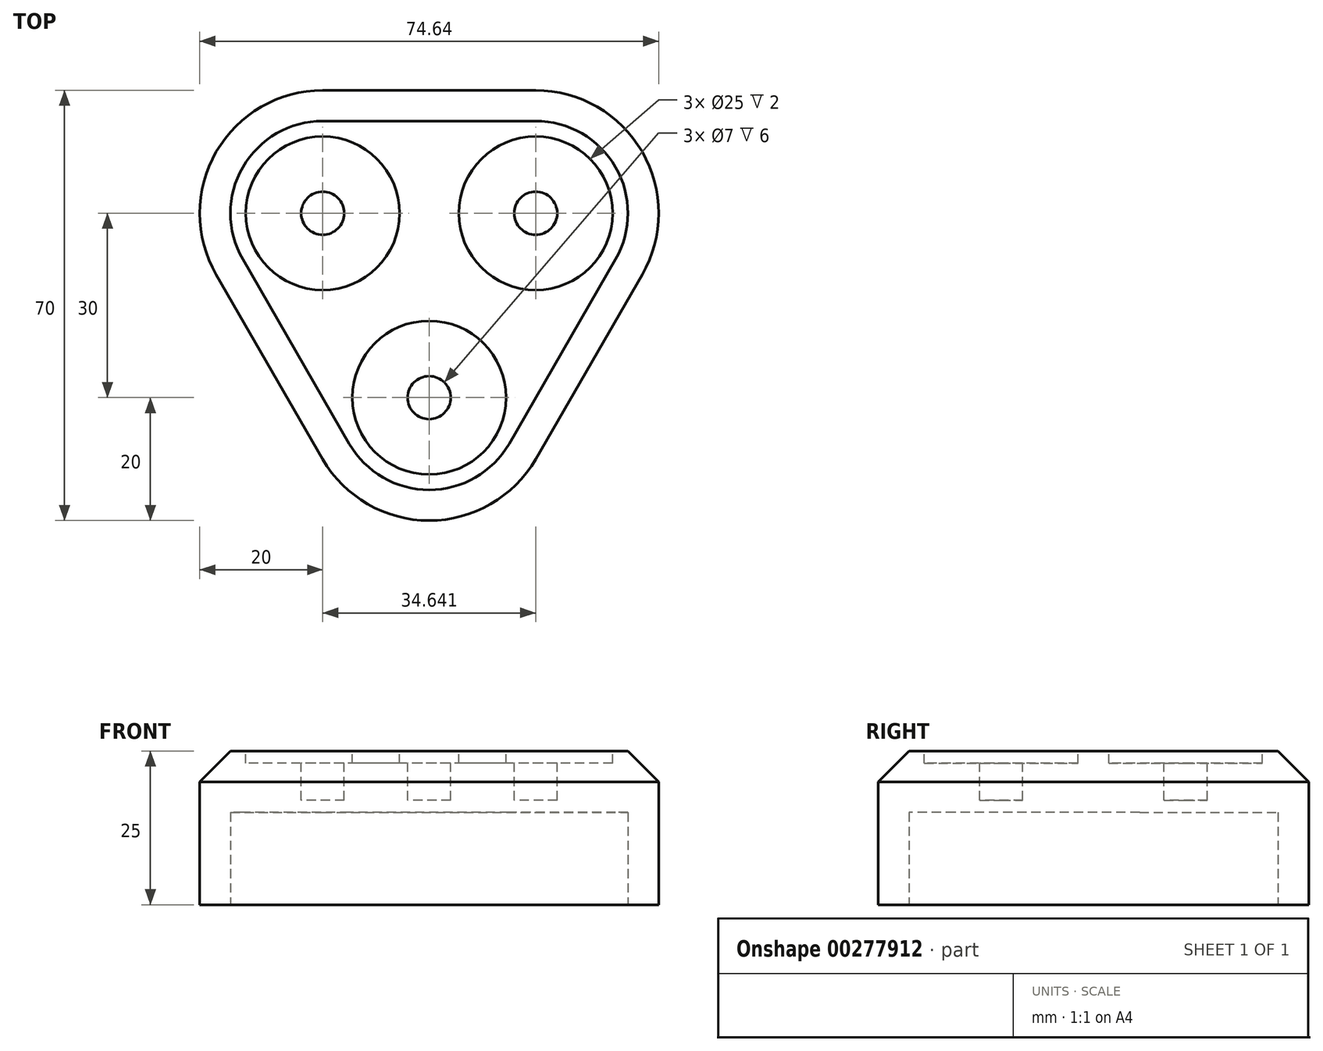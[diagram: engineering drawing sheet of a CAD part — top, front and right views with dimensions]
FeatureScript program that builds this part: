
annotation { "Feature Type Name" : "Feature", "Feature Type Description" : "" }
export const myFeature = defineFeature(function(context is Context, id is Id, definition is map)
    precondition{}
    {
        {
            var Q0;
            Q0=qCreatedBy(makeId("Top.planeOp"),FACE);
            var sketch = newSketch(context, id + "F0", { "sketchPlane" : qUnion([Q0])});
            skCircle(sketch, "E0.cCircle", {"center": v(0, 0) * mm, "radius": 30 * mm, "construction": true});
            skLineSegment(sketch, "E0.0", {"start": v(-17.32, 30) * mm, "end": v(17.32, 30) * mm});
            skLineSegment(sketch, "E0.1", {"start": v(34.64, 0) * mm, "end": v(17.32, -30) * mm});
            skLineSegment(sketch, "E0.2", {"start": v(-17.32, -30) * mm, "end": v(-34.64, 0) * mm});
            skPoint(sketch, "E0.0.midPoint", {"position": v(0, 30) * mm});
            skLineSegment(sketch, "E1", {"start": v(0, 0) * mm, "end": v(-51.96, 30) * mm, "construction": true});
            skCircle(sketch, "E2", {"center": v(-17.32, 10) * mm, "radius": 12.5 * mm, "construction": true});
            skCircle(sketch, "E3.1.0", {"center": v(0, -20) * mm, "radius": 12.5 * mm, "construction": true});
            skCircle(sketch, "E3.2.0", {"center": v(17.32, 10) * mm, "radius": 12.5 * mm, "construction": true});
            skLineSegment(sketch, "E4", {"start": v(-17.32, 10) * mm, "end": v(-17.32, 30) * mm, "construction": true});
            skPoint(sketch, "E5.visualSharp", {"position": v(-51.96, 30) * mm});
            skArc(sketch, "E5.filletArc", {"start": v(-17.32, 30) * mm, "mid": v(-34.64, 20) * mm, "end": v(-34.64, 0) * mm});
            skPoint(sketch, "E6.visualSharp", {"position": v(0, -60) * mm});
            skArc(sketch, "E6.filletArc", {"start": v(-17.32, -30) * mm, "mid": v(0, -40) * mm, "end": v(17.32, -30) * mm});
            skPoint(sketch, "E7.visualSharp", {"position": v(51.96, 30) * mm});
            skArc(sketch, "E7.filletArc", {"start": v(34.64, 0) * mm, "mid": v(34.64, 20) * mm, "end": v(17.32, 30) * mm});
            skSolve(sketch);
        }
        {
            var Q0;
            Q0 = qSketchRegion(id + "F0", true);
            extrude(context, id + "F1", {"entities" : qUnion([Q0]), "depth" : 25 * mm});
        }
        {
            var Q0;
            Q0=makeQuery(id+"F1.opExtrude","CAP_FACE",FACE,{"disambiguationData":[OSD([sQuery(id+"F0.wireOp",EDGE,"E0.0"),sQuery(id+"F0.wireOp",EDGE,"E0.1"),sQuery(id+"F0.wireOp",EDGE,"E0.2"),sQuery(id+"F0.wireOp",EDGE,"E5.filletArc"),sQuery(id+"F0.wireOp",EDGE,"E6.filletArc"),sQuery(id+"F0.wireOp",EDGE,"E7.filletArc")])],"isStart":false});
            var sketch = newSketch(context, id + "F2", { "sketchPlane" : qUnion([Q0])});
            skLineSegment(sketch, "E8", {"start": v(0, 0) * mm, "end": v(-34.64, 20) * mm, "construction": true});
            skCircle(sketch, "E9", {"center": v(-17.32, 10) * mm, "radius": 12.5 * mm});
            skCircle(sketch, "E10.1.0", {"center": v(0, -20) * mm, "radius": 12.5 * mm});
            skCircle(sketch, "E10.2.0", {"center": v(17.32, 10) * mm, "radius": 12.5 * mm});
            skPoint(sketch, "E10.center", {"position": v(0, 0) * mm});
            skSolve(sketch);
        }
        {
            var Q0;
            Q0 = qSketchRegion(id + "F2", true);
            extrude(context, id + "F3", {"entities" : qUnion([Q0]), "operationType" : NewBodyOperationType.REMOVE, "oppositeDirection" : true, "depth" : 2 * mm});
        }
        {
            var Q0;
            Q0=makeQuery(id+"F3.boolean.opBoolean","COPY",FACE,{"derivedFrom":makeQuery(id+"F3.opExtrude","CAP_FACE",FACE,{"disambiguationData":[OSD([sQuery(id+"F2.wireOp",EDGE,"E9")])],"isStart":false})});
            var sketch = newSketch(context, id + "F4", { "sketchPlane" : qUnion([Q0])});
            skCircle(sketch, "E11", {"center": v(-17.32, 10) * mm, "radius": 3.5 * mm});
            skCircle(sketch, "E12.1.0", {"center": v(0, -20) * mm, "radius": 3.5 * mm});
            skCircle(sketch, "E12.2.0", {"center": v(17.32, 10) * mm, "radius": 3.5 * mm});
            skPoint(sketch, "E12.center", {"position": v(0, 0) * mm});
            skSolve(sketch);
        }
        {
            var Q0;
            Q0 = qSketchRegion(id + "F4", true);
            extrude(context, id + "F5", {"entities" : qUnion([Q0]), "operationType" : NewBodyOperationType.REMOVE, "oppositeDirection" : true, "depth" : 6 * mm});
        }
        {
            var Q0;
            Q0=makeQuery(id+"F1.opExtrude","CAP_EDGE",EDGE,{"disambiguationData":[OSD([sQuery(id+"F0.wireOp",EDGE,"E0.1")])],"isStart":false});
            chamfer(context, id + "F6", {"entities" : qUnion([Q0]), "width" : 5 * mm, "tangentPropagation" : true});
        }
        {
            var Q0;
            Q0=makeQuery(id+"F1.opExtrude","CAP_FACE",FACE,{"disambiguationData":[OSD([sQuery(id+"F0.wireOp",EDGE,"E0.0"),sQuery(id+"F0.wireOp",EDGE,"E0.1"),sQuery(id+"F0.wireOp",EDGE,"E0.2"),sQuery(id+"F0.wireOp",EDGE,"E5.filletArc"),sQuery(id+"F0.wireOp",EDGE,"E6.filletArc"),sQuery(id+"F0.wireOp",EDGE,"E7.filletArc")])],"isStart":true});
            var sketch = newSketch(context, id + "F7", { "sketchPlane" : qUnion([Q0])});
            skArc(sketch, "E13.0", {"start": v(34.64, 0) * mm, "mid": v(34.64, -20) * mm, "end": v(17.32, -30) * mm, "construction": true});
            skLineSegment(sketch, "E14.0", {"start": v(-17.32, -30) * mm, "end": v(17.32, -30) * mm, "construction": true});
            skArc(sketch, "E15.0", {"start": v(-17.32, -30) * mm, "mid": v(-34.64, -20) * mm, "end": v(-34.64, 0) * mm, "construction": true});
            skLineSegment(sketch, "E16.0", {"start": v(-17.32, 30) * mm, "end": v(-34.64, 0) * mm, "construction": true});
            skArc(sketch, "E17.0", {"start": v(-17.32, 30) * mm, "mid": v(0, 40) * mm, "end": v(17.32, 30) * mm, "construction": true});
            skLineSegment(sketch, "E18.0", {"start": v(34.64, 0) * mm, "end": v(17.32, 30) * mm, "construction": true});
            skLineSegment(sketch, "E19.0", {"start": v(-13, 27.5) * mm, "end": v(-30.31, -2.5) * mm});
            skLineSegment(sketch, "E19.1", {"start": v(30.31, -2.5) * mm, "end": v(13, 27.5) * mm});
            skArc(sketch, "E19.2", {"start": v(30.31, -2.5) * mm, "mid": v(30.31, -17.5) * mm, "end": v(17.32, -25) * mm});
            skArc(sketch, "E19.3", {"start": v(-13, 27.5) * mm, "mid": v(0, 35) * mm, "end": v(13, 27.5) * mm});
            skLineSegment(sketch, "E19.4", {"start": v(-17.32, -25) * mm, "end": v(17.32, -25) * mm});
            skArc(sketch, "E19.5", {"start": v(-17.32, -25) * mm, "mid": v(-30.31, -17.5) * mm, "end": v(-30.31, -2.5) * mm});
            skSolve(sketch);
        }
        {
            var Q0;
            Q0 = qSketchRegion(id + "F7", true);
            extrude(context, id + "F8", {"entities" : qUnion([Q0]), "operationType" : NewBodyOperationType.REMOVE, "oppositeDirection" : true, "depth" : 15 * mm});
        }
    });
